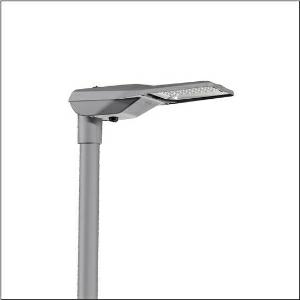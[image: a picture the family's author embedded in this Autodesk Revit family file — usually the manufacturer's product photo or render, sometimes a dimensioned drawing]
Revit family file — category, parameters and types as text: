
# Revit family: streetlight_sl_21_iq_mini___st1_0a_5xe2d31y08hb_7569
name_source: partatom
category: Lighting Fixtures
units: mm (PartAtom-declared; Revit-internal decimal feet)

## family parameters
Cut with Voids When Loaded = No
Host = Face
Light Source = No
Part Type = Normal
Room Calculation Point = No
Round Connector Dimension = Use Diameter
Shared = No

## types (1)
- --- (1 x LED, 9750 lm, 71 W, 3000K)
    Apparent Load = 71 VA
    CIE Flux Codes = 37 72 97 100 100
    Color Rendering = 70
    Color Temperature = 3000K
    Default Elevation = 1800 mm
    Description = Streetlight SL 21 iQ mini, mast luminaire, primary light control with lens, of PMMA, primary optical cover: cover, of toughened safety glass, transparent, light distribution: ST1.0a, light emission: direct distribution, primary light characteristic: asymmetric, installation type: post-top, side-entry, LED, High Power LED, rated luminous flux: 9.750lm, luminous efficacy: 137lm/W, light colour: 730, colour temperature: 3000K, control gear: iQ-Street Remote, D4i with power reduction, control: pre-setting: logarithmic dimming characteristic, Street-Remote, Auto-Match, Temp-Guard, Lumen-Switch, Night-Set, Smart-Wire, Light-Fading, Desk-Remote (wireless, voltage-free reading and setting of iQ features in the workshop via application-optimized NFC function/RFID function), optimised constant luminous flux control (CLO 2.0), mains connection: 220..240V, AC, 50/60Hz, start of lifetime: 71W, end of service life: 75W, reduction: 30W, luminaire housing, of diecast aluminium, powder-coated, Siteco® metallic grey (DB 702S), corrosivity category C5 mid according to DIN EN ISO 12944, please order mast flange separately, inclination adjustable: 0°, 5°, 10°, 15°, sealing non-destructively replaceable, multi-level sealing system, length: 628mm, width: 235mm, height: 110mm, mast flange for spigot size: 42mm (side-entry): 5XC10008XM4, 60/48mm (side-entry/post-top): 5XC10108XM2, 76/60mm (side-entry/post-top): 5XC10108XM1, mounting height: 4..8m, Smart Interface below and above, protection rating (complete): IP66, insulation class (complete): insulation class II (safety insulation), certification: CE, ENEC, ENEC+, VDE, impact resistance: IK10, permissible operating ambient temperature for outdoor applications: -40..+50°C, standard-compliant lighting for roads and squares, packaging unit: 1 piece

Light Distribution: ST1.0a
    Height = 110 mm
    Lamp = 1 x LED
    Lamp Light Flux = 9750 lm
    Lamp Power = 71 W
    Lamp count = 1
    Length = 625 mm
    Luminous efficacy = 137 lm/W
    Manufacturer = Siteco
    ModVariant = No
    Model = 5XE2D31Y08HB
    Number of Poles = 1
    OnlyDefault = Yes
    Power Factor = 1
    Product Name = Streetlight SL 21 iQ mini | ST1.0a
    Product group = mast luminaire | pylon top
    ProductGroupID = 6100
    Protection Class = Protection class II
    Protection Degree = IP 66
    RLX_Detail_Level = 1
    RLX_Emergency_Light_Flux = 0 lm
    RLX_Emergency_Type = 0
    RLX_Emergency_Type_DB = No
    RlxData = <blob elided: 94485 chars, md5=f82b0379>
    Socket = socket
    Standby Power = 0 W
    System Light Flux = 9750 lm
    System Power = 71 W
    Type Comments = factory setting: luminous flux: 100 % | dim-lin: 254 | 716 mA
    Type Image = l_1003514.jpg
    URL = http://relux.com
    VarID = @adj_136353
    Voltage = 0 V
    Weight = 0.00 kg
    Width = 234 mm

## geometry (parser evidence)
native form markers: Blend x4, Sweep x10
no freeform markers — native parametric forms only
